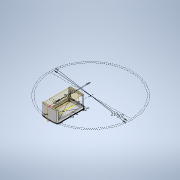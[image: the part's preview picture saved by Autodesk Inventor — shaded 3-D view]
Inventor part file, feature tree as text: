
AUTODESK INVENTOR PART (.ipt)
format: ipt  version: 2020 (Build 240168000, 168)  size: 234,496 bytes
history: native  units: mm
features: projected_geometry x12, extrude x6, sketch x5, other x3
ambient origin geometry x8: Origin, YZ Plane, XZ Plane, XY Plane, X Axis, Y Axis, Z Axis, Center Point
bodies: Body1 (feature_tree)
feature tree (26):
  other  "Твердое тело1"
  sketch  "Эскиз1"
  extrude  "Выдавливание3"  Depth=202.0mm
  other  "РабПлоскость1"
  extrude  "Выдавливание1"  Depth=35.0mm
  other  "РабПлоскость2"
  sketch  "Эскиз2"
  extrude  "Выдавливание4"  Depth=65.0mm
  extrude  "Выдавливание5"  Depth=2.0mm
  sketch  "Эскиз4"
  extrude  "Выдавливание6"  Depth=2.0mm
  extrude  "Выдавливание7"  Depth=2.0mm
  projected_geometry  "Спроецированная петля1"
  projected_geometry  "Спроецированная петля7"
  projected_geometry  "Спроецированная петля8"
  sketch  "Эскиз3"
  projected_geometry  "Спроецированная петля9"
  projected_geometry  "Спроецированная петля10"
  projected_geometry  "Спроецированная петля11"
  projected_geometry  "Спроецированная петля12"
  sketch  "Эскиз5"
  projected_geometry  "Спроецированная петля13"
  projected_geometry  "Спроецированная петля14"
  projected_geometry  "Спроецированная петля15"
  projected_geometry  "Спроецированная петля16"
  projected_geometry  "Спроецированная петля17"
